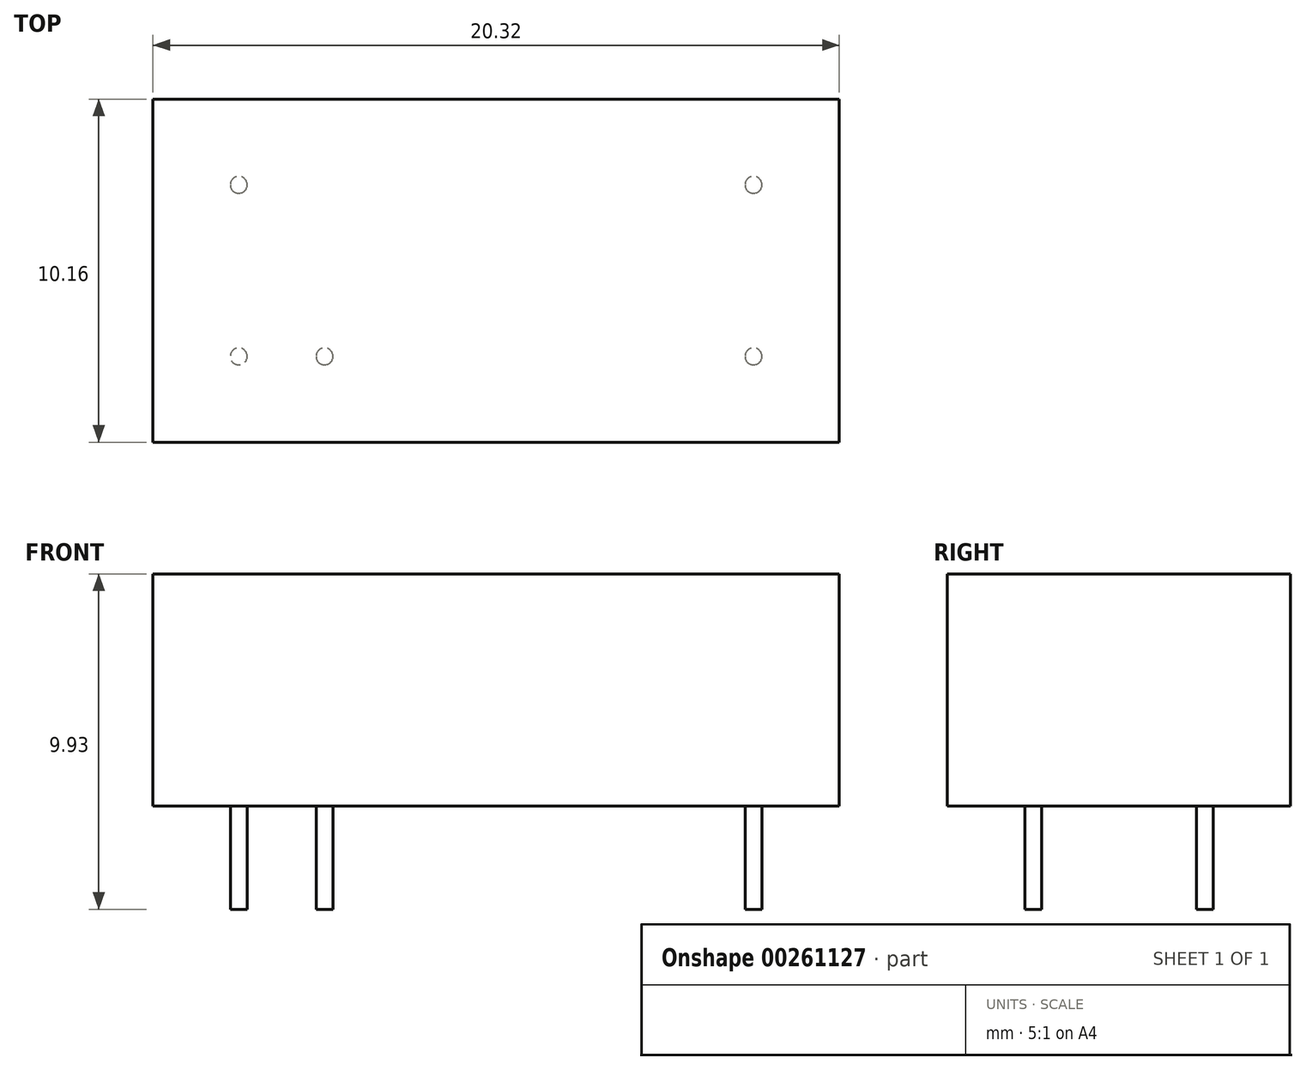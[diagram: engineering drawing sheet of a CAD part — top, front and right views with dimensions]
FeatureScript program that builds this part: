
annotation { "Feature Type Name" : "Feature", "Feature Type Description" : "" }
export const myFeature = defineFeature(function(context is Context, id is Id, definition is map)
    precondition{}
    {
        {
            var Q0;
            Q0=qCreatedBy(makeId("Top.planeOp"),FACE);
            var sketch = newSketch(context, id + "F0", { "sketchPlane" : qUnion([Q0])});
            skLineSegment(sketch, "E0.bottom", {"start": v(10.16, 5.08) * mm, "end": v(-10.16, 5.08) * mm});
            skLineSegment(sketch, "E0.top", {"start": v(10.16, -5.08) * mm, "end": v(-10.16, -5.08) * mm});
            skLineSegment(sketch, "E0.left", {"start": v(10.16, 5.08) * mm, "end": v(10.16, -5.08) * mm});
            skLineSegment(sketch, "E0.right", {"start": v(-10.16, 5.08) * mm, "end": v(-10.16, -5.08) * mm});
            skPoint(sketch, "E0.middle", {"position": v(0, 0) * mm});
            skSolve(sketch);
        }
        {
            var Q0;
            Q0 = qSketchRegion(id + "F0", true);
            extrude(context, id + "F1", {"entities" : qUnion([Q0]), "depth" : 6.88 * mm});
        }
        {
            var Q0;
            Q0=makeQuery(id+"F1.opExtrude","CAP_FACE",FACE,{"disambiguationData":[OSD([sQuery(id+"F0.wireOp",EDGE,"E0.bottom"),sQuery(id+"F0.wireOp",EDGE,"E0.top"),sQuery(id+"F0.wireOp",EDGE,"E0.left"),sQuery(id+"F0.wireOp",EDGE,"E0.right")])],"isStart":true});
            var sketch = newSketch(context, id + "F2", { "sketchPlane" : qUnion([Q0])});
            skCircle(sketch, "E1", {"center": v(-7.62, 2.54) * mm, "radius": 0.25 * mm});
            skCircle(sketch, "E2", {"center": v(-5.08, 2.54) * mm, "radius": 0.25 * mm});
            skCircle(sketch, "E3", {"center": v(-7.62, -2.54) * mm, "radius": 0.25 * mm});
            skCircle(sketch, "E4", {"center": v(7.62, 2.54) * mm, "radius": 0.25 * mm});
            skCircle(sketch, "E5", {"center": v(7.62, -2.54) * mm, "radius": 0.25 * mm});
            skLineSegment(sketch, "E6", {"start": v(7.62, 2.54) * mm, "end": v(7.62, -2.54) * mm});
            skLineSegment(sketch, "E7", {"start": v(-7.62, 2.54) * mm, "end": v(-7.62, -2.54) * mm});
            skSolve(sketch);
        }
        {
            var Q0;
            Q0 = qSketchRegion(id + "F2", true);
            extrude(context, id + "F3", {"entities" : qUnion([Q0]), "operationType" : NewBodyOperationType.ADD, "depth" : 3.05 * mm});
        }
    });
